# Revit family: IRB 400 E3 ErP AC_7890117
name_source: partatom
category: Mechanical Equipment
revit_build: Autodesk Revit MEP 2014 (Build: 20130308_1515(x64)
units: mm (PartAtom-declared; Revit-internal decimal feet)

## types (1)
- IRB 400 E3 ErP AC
    Capacitor = - µF
    Current = 2 A
    Depth = 567 mm  [stored 1.86024 ft]
    Description = Insulated duct fans with circular connections
    Diameter = 400 mm  [stored 1.31234 ft]
    Frequency = 50 Hz
    Height = 808 mm  [stored 2.65092 ft]
    Main Material = Steel, Galvanized
    Max. temperature of transported air = 40 °C
    Max. temperature of transported air when speed controlled = 40 °C
    Phase = 3
    Power = 739 W
    Sound pressure level at 3 m = 53dB(A)
    Speed = 1440 rpm
    Voltage = 400 V
    Voltage range = 380-415 V
    Weight = 68.40 kg
    Width = 995 mm  [stored 3.26444 ft]
    Wiring diagram = Y 4040004 / Δ4040003

note: [stored X ft] marks values corroborated as IEEE doubles in the binary element streams (Revit-internal decimal feet)

## geometry (parser evidence)
native form markers: Sweep x4
no freeform markers — native parametric forms only
